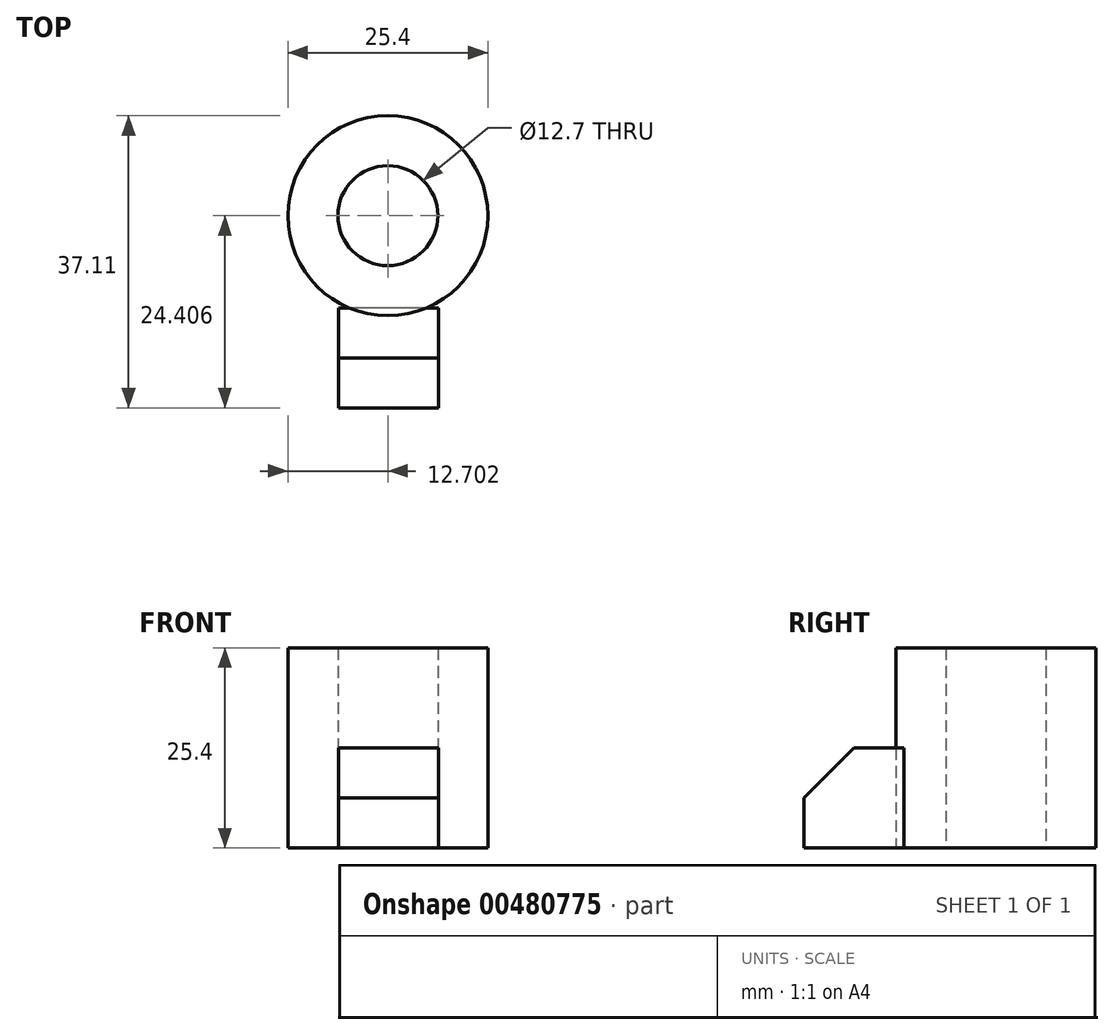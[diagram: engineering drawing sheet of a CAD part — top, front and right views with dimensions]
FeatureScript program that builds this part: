
annotation { "Feature Type Name" : "Feature", "Feature Type Description" : "" }
export const myFeature = defineFeature(function(context is Context, id is Id, definition is map)
    precondition{}
    {
        {
            var Q0;
            Q0=qCreatedBy(makeId("Top.planeOp"),FACE);
            var sketch = newSketch(context, id + "F0", { "sketchPlane" : qUnion([Q0])});
            skCircle(sketch, "E0", {"center": v(6.27, -1) * mm, "radius": 12.7 * mm});
            skCircle(sketch, "E1", {"center": v(6.27, -1) * mm, "radius": 6.35 * mm});
            skSolve(sketch);
        }
        {
            var Q0;
            Q0=qCreatedBy(makeId("Right.planeOp"),FACE);
            var sketch = newSketch(context, id + "F1", { "sketchPlane" : qUnion([Q0])});
            skLineSegment(sketch, "E2", {"start": v(-12.7, 12.7) * mm, "end": v(-12.7, 0) * mm});
            skLineSegment(sketch, "E3", {"start": v(-12.7, 0) * mm, "end": v(-25.4, 0) * mm});
            skLineSegment(sketch, "E4", {"start": v(-25.4, 0) * mm, "end": v(-25.4, 6.35) * mm});
            skLineSegment(sketch, "E5", {"start": v(-25.4, 6.35) * mm, "end": v(-19.05, 12.7) * mm});
            skLineSegment(sketch, "E6", {"start": v(-19.05, 12.7) * mm, "end": v(-12.7, 12.7) * mm});
            skSolve(sketch);
        }
        {
            var Q0;
            Q0=makeQuery(id+"F1.imprint","IMPRINT",FACE,{"disambiguationData":[TD([[makeQuery(id+"F1.imprint","IMPRINT",EDGE,{"derivedFrom":sQuery(id+"F1.wireOp",EDGE,"E2")}),-1.0]])]});
            extrude(context, id + "F2", {"entities" : qUnion([Q0]), "depth" : 12.7 * mm});
        }
        {
            var Q0;
            Q0=makeQuery(id+"F0.imprint","IMPRINT",FACE,{"disambiguationData":[TD([[makeQuery(id+"F0.imprint","IMPRINT",EDGE,{"derivedFrom":sQuery(id+"F0.wireOp",EDGE,"E0")}),1.0]])]});
            extrude(context, id + "F3", {"entities" : qUnion([Q0]), "depth" : 25.4 * mm});
        }
    });
